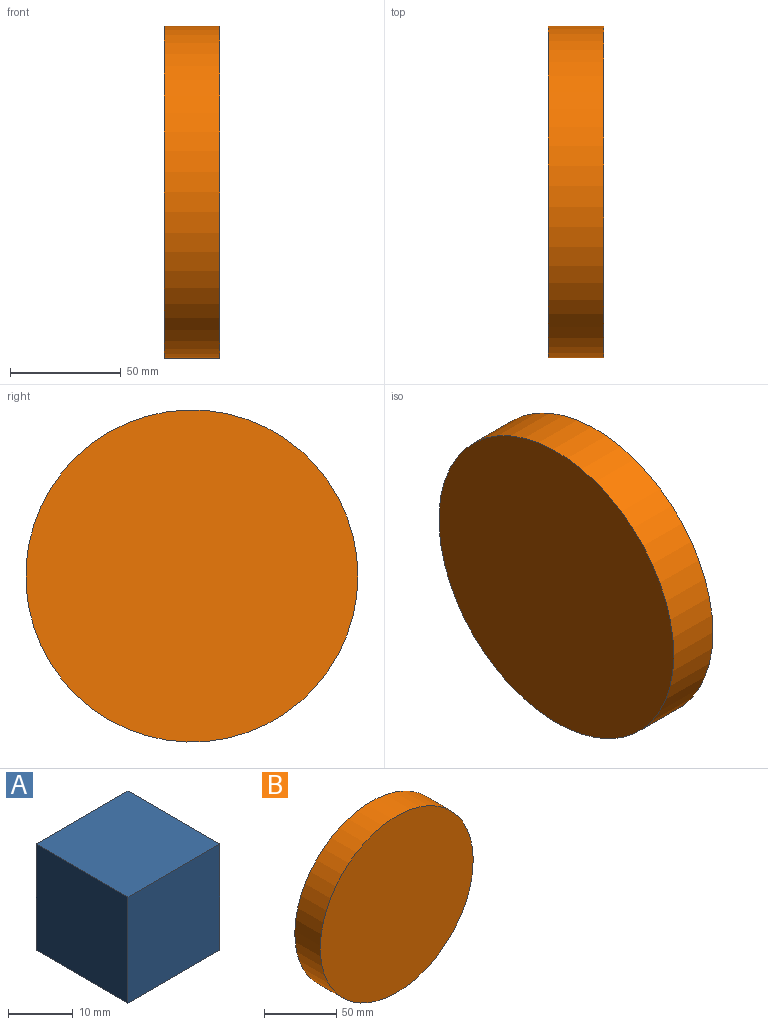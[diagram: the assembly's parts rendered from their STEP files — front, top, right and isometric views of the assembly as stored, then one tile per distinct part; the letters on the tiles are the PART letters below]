
ASSEMBLY  parts=2 mates=1
PART A: 6 faces, bbox 20x20x20 mm
  f0: plane 20x20mm, normal (0,0,-1), area 400mm2, adj f1,f3,f4,f5
  f1: plane 20x20mm, normal (1,0,0), area 400mm2, adj f0,f2,f4,f5
  f2: plane 20x20mm, normal (0,0,1), area 400mm2, adj f1,f3,f4,f5
  f3: plane 20x20mm, normal (-1,0,0), area 400mm2, adj f0,f2,f4,f5
  f4: plane 20x20mm, normal (0,-1,0), area 400mm2, adj f0,f1,f2,f3
  f5: plane 20x20mm, normal (0,1,0), area 400mm2, adj f0,f1,f2,f3
PART B: 3 faces, bbox 150x25x150 mm
  f0: cylinder r=75mm len=150mm, axis (0,1,0), area 11781mm2, adj f1,f2
  f1: plane 150x150mm, normal (0,-1,0), area 17671.5mm2, adj f0
  f2: plane 150x150mm, normal (0,1,0), area 17671.5mm2, adj f0
PLACE A t=(17.37,0.97,13.65)mm
PLACE B rot(axis=(-0.58,0.58,0.58),120deg) t=(-7.63,-11.17,-21.79)mm
MATE planar B.f0 <-> A.f1  axis (1,0,0) through (17.37,-11.17,-21.79)mm
